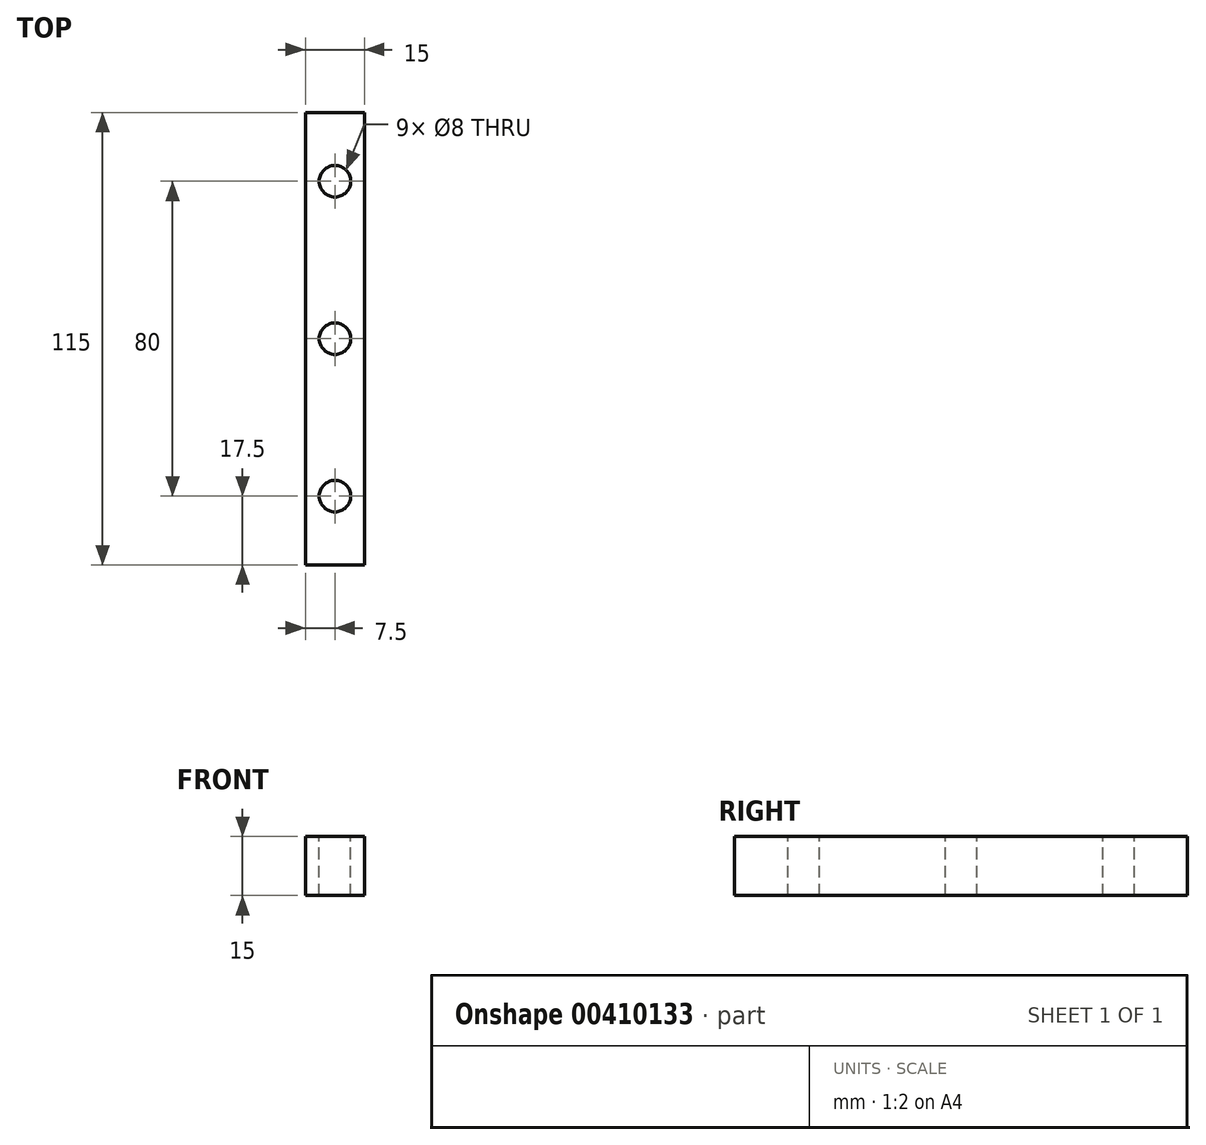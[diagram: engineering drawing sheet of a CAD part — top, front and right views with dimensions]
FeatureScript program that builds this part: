
annotation { "Feature Type Name" : "Feature", "Feature Type Description" : "" }
export const myFeature = defineFeature(function(context is Context, id is Id, definition is map)
    precondition{}
    {
        {
            var Q0;
            Q0=qCreatedBy(makeId("Front.planeOp"),FACE);
            var sketch = newSketch(context, id + "F0", { "sketchPlane" : qUnion([Q0])});
            skLineSegment(sketch, "E0.bottom", {"start": v(0, 0) * mm, "end": v(15, 0) * mm});
            skLineSegment(sketch, "E0.top", {"start": v(0, 15) * mm, "end": v(15, 15) * mm});
            skLineSegment(sketch, "E0.left", {"start": v(0, 0) * mm, "end": v(0, 15) * mm});
            skLineSegment(sketch, "E0.right", {"start": v(15, 0) * mm, "end": v(15, 15) * mm});
            skSolve(sketch);
        }
        {
            var Q0;
            Q0=makeQuery(id+"F0.imprint","IMPRINT",FACE,{"disambiguationData":[TD([[makeQuery(id+"F0.imprint","IMPRINT",EDGE,{"derivedFrom":sQuery(id+"F0.wireOp",EDGE,"E0.bottom")}),1.0]])]});
            extrude(context, id + "F1", {"entities" : qUnion([Q0]), "depth" : 115 * mm});
        }
        {
            var Q0;
            Q0=makeQuery(id+"F1.opExtrude","SWEPT_FACE",FACE,{"disambiguationData":[OSD([sQuery(id+"F0.wireOp",EDGE,"E0.top")])]});
            var sketch = newSketch(context, id + "F2", { "sketchPlane" : qUnion([Q0])});
            skLineSegment(sketch, "E1", {"start": v(7.5, 0) * mm, "end": v(7.5, -115) * mm, "construction": true});
            skCircle(sketch, "E2", {"center": v(7.5, -17.5) * mm, "radius": 4 * mm});
            skCircle(sketch, "E3.0.1.0", {"center": v(7.5, -57.5) * mm, "radius": 4 * mm});
            skCircle(sketch, "E3.0.2.0", {"center": v(7.5, -97.5) * mm, "radius": 4 * mm});
            skLineSegment(sketch, "E3.direction1", {"start": v(7.5, -17.5) * mm, "end": v(32.5, -17.5) * mm, "construction": true});
            skLineSegment(sketch, "E3.direction2", {"start": v(7.5, -17.5) * mm, "end": v(7.5, -57.5) * mm, "construction": true});
            skSolve(sketch);
        }
        {
            var Q0;
            Q0 = qSketchRegion(id + "F2", true);
            extrude(context, id + "F3", {"entities" : qUnion([Q0]), "operationType" : NewBodyOperationType.REMOVE, "endBound" : BoundingType.THROUGH_ALL, "oppositeDirection" : true, "depth" : 25 * mm});
        }
    });
